# Revit family: Telford Tilt Top Rectangular 700 Deep
name_source: partatom
category: Furniture
revit_build: Autodesk Revit 2016 (Build: 20160525_1230(x64)
units: mm (PartAtom-declared; Revit-internal decimal feet)

## family parameters
Always vertical = Yes
Cut with Voids When Loaded = No
OmniClass Number = 23.40.20.00
OmniClass Title = General Furniture and Specialties
Room Calculation Point = No
Shared = No
Work Plane-Based = No

## types (6) — shared parameters
Assembly Code = E2020200
Frame = Gresham - Black Metal
Manufacturer = Gresham Office Furniture
Range = TELFORD TILT TOP
Table Top = Gresham - White MFC
URL = www.gof.co.uk

## per-type parameters (varying)
| type | Product Code | Width |
| 1800 x 700 | DRMT187Z | 1800 mm |
| 1600 x 700 | DRMT167Z | 1600 mm  [stored 5.24934 ft] |
| 1400 x 700 | DRMT147Z | 1400 mm  [stored 4.59318 ft] |
| 1200 x 700 | DRMT127Z | 1200 mm |
| 1000 x 700 | DRMT107Z | 1000 mm  [stored 3.28084 ft] |
| 800 x 700 | DRMT087Z | 800 mm  [stored 2.62467 ft] |

note: [stored X ft] marks values corroborated as IEEE doubles in the binary element streams (Revit-internal decimal feet)

## geometry (parser evidence)
native form markers: Blend x4, Sweep x11
no freeform markers — native parametric forms only
